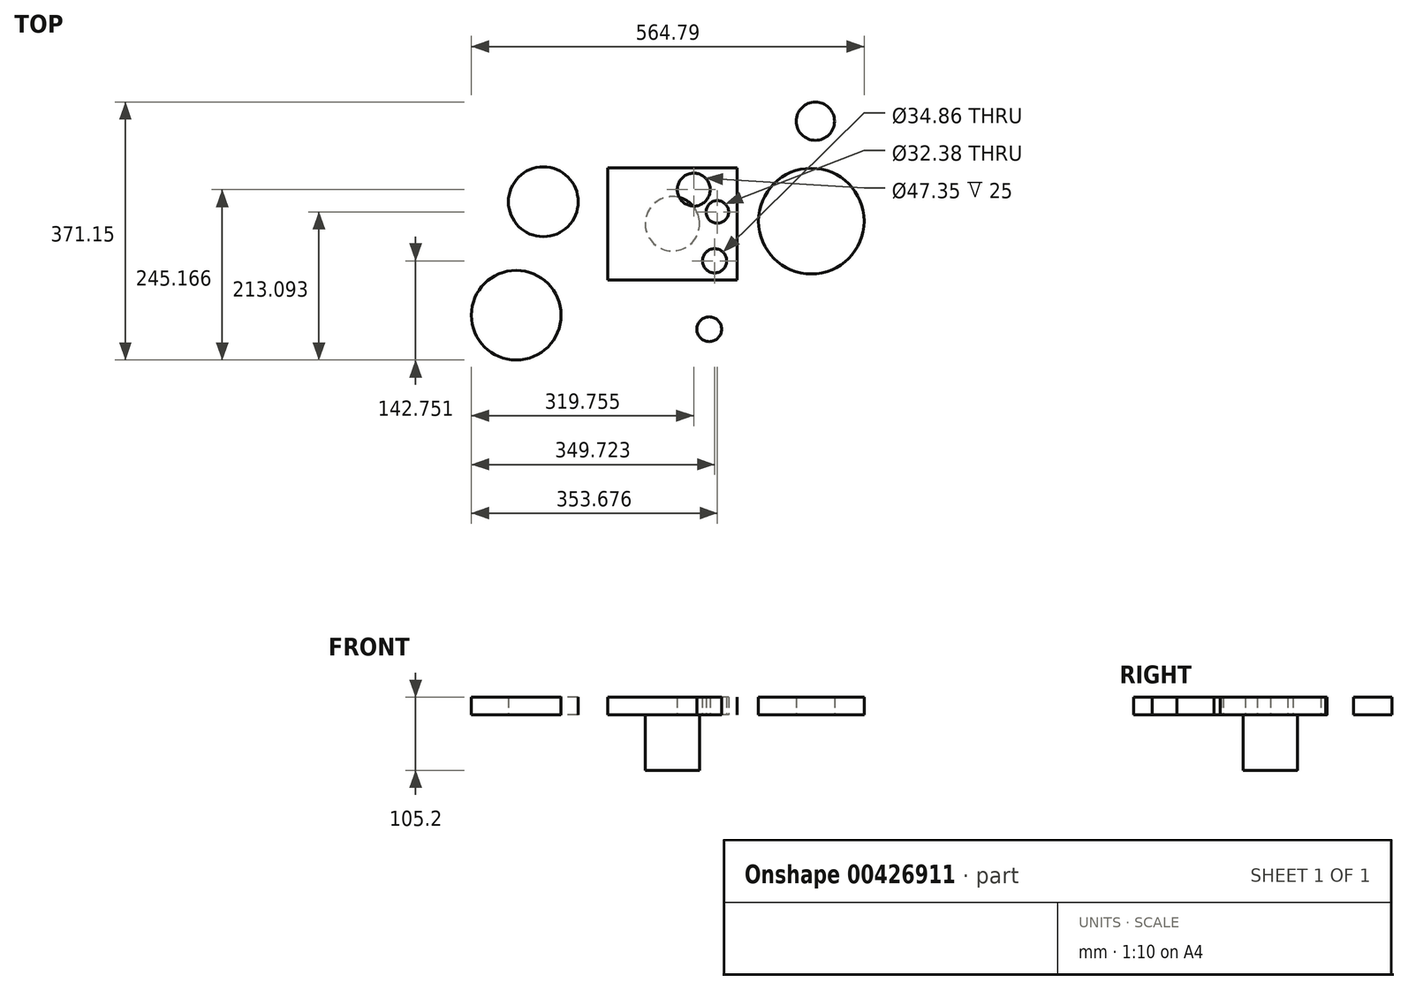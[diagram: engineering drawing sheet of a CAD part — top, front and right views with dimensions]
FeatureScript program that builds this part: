
annotation { "Feature Type Name" : "Feature", "Feature Type Description" : "" }
export const myFeature = defineFeature(function(context is Context, id is Id, definition is map)
    precondition{}
    {
        {
            var Q0;
            Q0=qCreatedBy(makeId("Top.planeOp"),FACE);
            var sketch = newSketch(context, id + "F0", { "sketchPlane" : qUnion([Q0])});
            skCircle(sketch, "E0", {"center": v(0, 0) * mm, "radius": 39.09 * mm});
            skSolve(sketch);
        }
        {
            var Q0;
            Q0 = qSketchRegion(id + "F0", true);
            extrude(context, id + "F1", {"entities" : qUnion([Q0]), "depth" : 80.2 * mm});
        }
        {
            var Q0;
            Q0=makeQuery(id+"F1.opExtrude","CAP_FACE",FACE,{"disambiguationData":[OSD([sQuery(id+"F0.wireOp",EDGE,"E0")])],"isStart":false});
            var sketch = newSketch(context, id + "F2", { "sketchPlane" : qUnion([Q0])});
            skLineSegment(sketch, "E1.bottom", {"start": v(93.02, -80.73) * mm, "end": v(-93.02, -80.73) * mm});
            skLineSegment(sketch, "E1.top", {"start": v(93.02, 80.73) * mm, "end": v(-93.02, 80.73) * mm});
            skLineSegment(sketch, "E1.left", {"start": v(93.02, -80.73) * mm, "end": v(93.02, 80.73) * mm});
            skLineSegment(sketch, "E1.right", {"start": v(-93.02, -80.73) * mm, "end": v(-93.02, 80.73) * mm});
            skPoint(sketch, "E1.middle", {"position": v(0, 0) * mm});
            skCircle(sketch, "E2", {"center": v(60.58, -53.32) * mm, "radius": 17.43 * mm});
            skCircle(sketch, "E3", {"center": v(64.54, 17.02) * mm, "radius": 16.2 * mm});
            skCircle(sketch, "E4", {"center": v(30.61, 49.1) * mm, "radius": 23.68 * mm});
            skCircle(sketch, "E5", {"center": v(199.66, 3.85) * mm, "radius": 75.99 * mm});
            skCircle(sketch, "E6", {"center": v(205.57, 147.55) * mm, "radius": 27.53 * mm});
            skCircle(sketch, "E7", {"center": v(-224.64, -131.58) * mm, "radius": 64.5 * mm});
            skCircle(sketch, "E8", {"center": v(52.9, -151.68) * mm, "radius": 17.81 * mm});
            skCircle(sketch, "E9", {"center": v(-185.71, 31.68) * mm, "radius": 50.15 * mm});
            skSolve(sketch);
        }
        {
            var Q0;
            Q0 = qSketchRegion(id + "F2", true);
            extrude(context, id + "F3", {"entities" : qUnion([Q0]), "operationType" : NewBodyOperationType.ADD, "depth" : 25 * mm});
        }
    });
